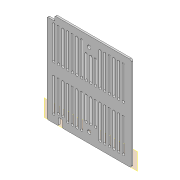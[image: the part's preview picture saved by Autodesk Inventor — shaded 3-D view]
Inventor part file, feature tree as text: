
AUTODESK INVENTOR PART (.ipt)
format: ipt  version: 2020 (Build 240168000, 168)  size: 462,848 bytes
history: native  units: mm
features: other x9, extrude x7, sketch x7, fillet x3, mirror x1
ambient origin geometry x8: Origin, YZ Plane, XZ Plane, XY Plane, X Axis, Y Axis, Z Axis, Center Point
bodies: Body1 (feature_tree)
feature tree (27):
  other  "Sólido1"
  other  "Plano de trabalho1"
  extrude  "Extrusão1"  Depth=0.5mm
  extrude  "Extrusão2"  Depth=1.0mm
  fillet  "Arredondamento1"  Radius=0.5mm
  extrude  "Extrusão3"  Depth=4.5mm
  extrude  "Extrusão4"  Depth=4.5mm
  fillet  "Arredondamento2"  Radius=10.0mm
  extrude  "Extrusão5"  Depth=18.0mm
  mirror  "Espelhamento1"
  extrude  "Extrusão6"  Depth=23.0mm
  extrude  "Extrusão7"  Depth=42.0mm
  fillet  "Arredondamento3"  Radius=42.0mm
  sketch  "Esboço1"  dims[d0=0.5mm d1=0.5mm]
  other  "Referência1"
  other  "Referência2"
  sketch  "Esboço2"  dims[d2=1.0mm d3=1.0mm d4=0.5mm]
  sketch  "Esboço3"  dims[d5=0.5mm d6=4.5mm]
  other  "Contorno projetado1"
  other  "Contorno projetado2"
  sketch  "Esboço4"  dims[d7=0.5mm d8=4.5mm d9=10.0mm]
  sketch  "Esboço5"  dims[d10=10.0mm d11=18.0mm]
  sketch  "Esboço6"  dims[d12=23.0mm d13=23.0mm]
  sketch  "Esboço7"  dims[d14=31.0mm d15=42.0mm d16=42.0mm d17=31.0mm d18=31.0mm d19=3.2mm d20=3.2mm d21=70.0mm d23=6.0mm d24=10.0mm d26=10.0mm d28=2.2mm d29=0.0mm d30=3.2mm d31=6.0mm d32=30.0mm d34=6.0mm d35=10.0mm d37=10.0mm d39=3.2mm d40=6.0mm d41=50.0mm d43=6.0mm d44=10.0mm d46=10.0mm d48=20.0mm d50=6.0mm d51=10.0mm d53=10.0mm d55=14.0mm d56=14.0mm d57=3.0mm d58=0.0mm d59=2.2mm d60=8.0mm d61=0.0mm d62=3.0mm d63=100.0mm d64=0.0mm d65=2.0mm d66=10.0mm d67=20.0mm d68=0.0mm d69=0.0mm d70=19.8mm d71=9.5mm d72=5.0mm d73=2.0mm d74=0.0mm d75=3.0mm d76=0.0mm d77=10.0mm d78=6.0mm d79=1.0mm]
  other  "Calorímetro.iam"
  other  "suporte_fechamento:2"
  other  "suporte_fechamento:3"
